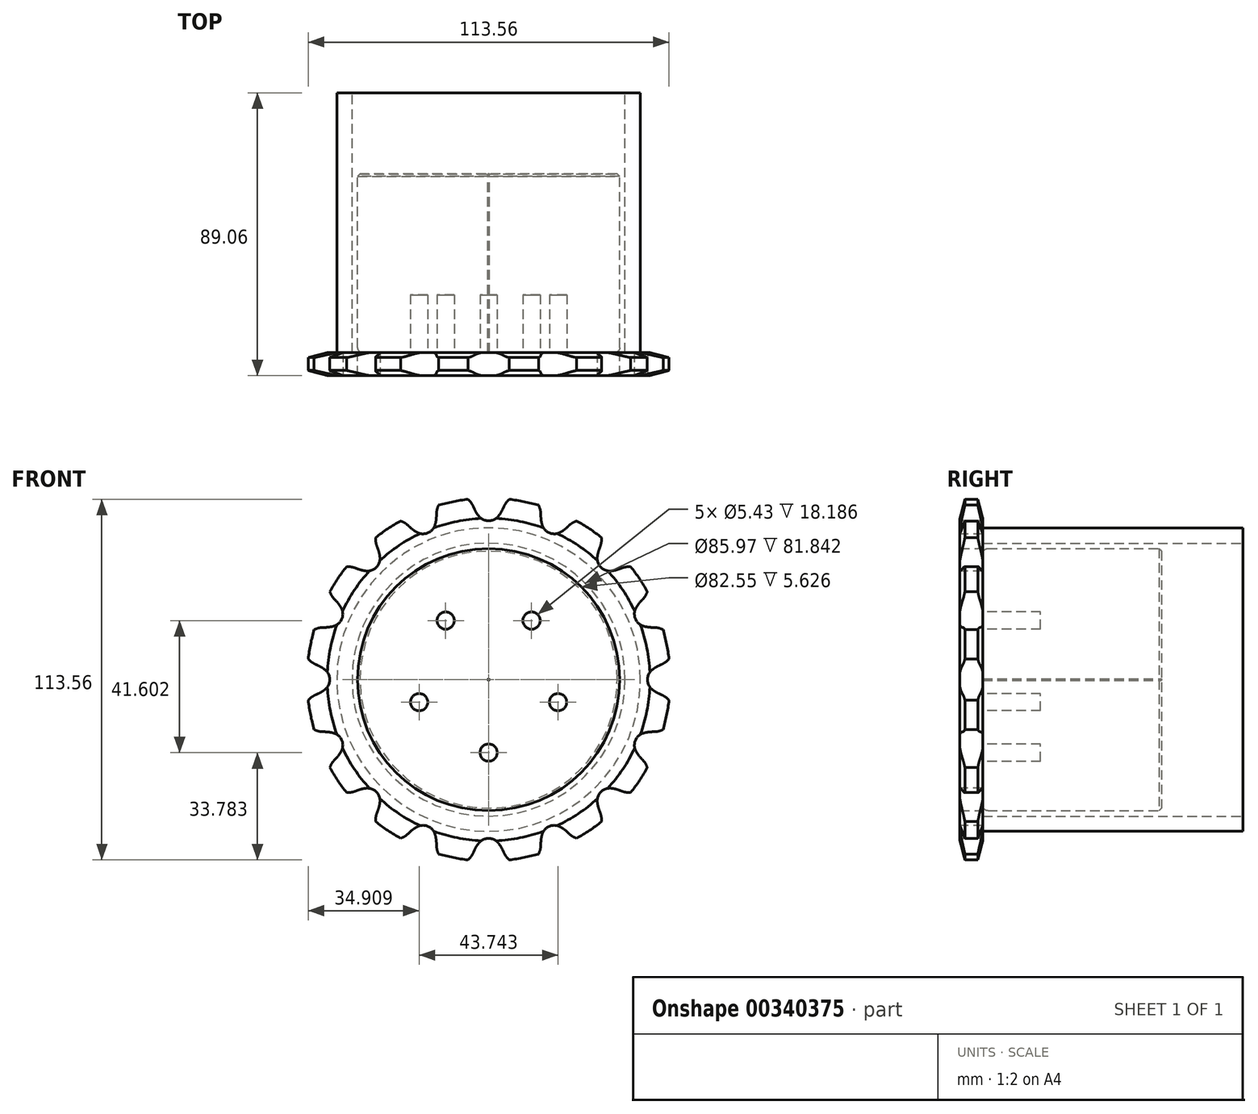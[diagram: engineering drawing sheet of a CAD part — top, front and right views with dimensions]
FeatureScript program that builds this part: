
annotation { "Feature Type Name" : "Feature", "Feature Type Description" : "" }
export const myFeature = defineFeature(function(context is Context, id is Id, definition is map)
    precondition{}
    {
        {
            var Q0;
            Q0=qCreatedBy(makeId("Right.planeOp"),FACE);
            var sketch = newSketch(context, id + "F0", { "sketchPlane" : qUnion([Q0])});
            skLineSegment(sketch, "E0", {"start": v(41.18, 0) * mm, "end": v(-36.1, 0) * mm, "construction": true});
            skLineSegment(sketch, "E1.bottom", {"start": v(-22.32, 0.21) * mm, "end": v(-15.1, 0.21) * mm});
            skLineSegment(sketch, "E1.top", {"start": v(-22.32, 57.15) * mm, "end": v(-15.1, 57.15) * mm});
            skLineSegment(sketch, "E1.left", {"start": v(-22.32, 0.21) * mm, "end": v(-22.32, 57.15) * mm});
            skLineSegment(sketch, "E1.right", {"start": v(-15.1, 0.21) * mm, "end": v(-15.1, 57.15) * mm});
            skLineSegment(sketch, "E2.bottom", {"start": v(-22.32, 0.21) * mm, "end": v(41.18, 0.21) * mm});
            skLineSegment(sketch, "E2.top", {"start": v(-22.32, 41.27) * mm, "end": v(41.18, 41.27) * mm});
            skLineSegment(sketch, "E2.left", {"start": v(-22.32, 0.21) * mm, "end": v(-22.32, 41.27) * mm});
            skLineSegment(sketch, "E2.right", {"start": v(41.18, 0.21) * mm, "end": v(41.18, 41.28) * mm});
            skLineSegment(sketch, "E3.MirrorCS", {"start": v(-22.32, -0.21) * mm, "end": v(-15.1, -0.21) * mm});
            skLineSegment(sketch, "E4.MirrorCS", {"start": v(41.18, -0.21) * mm, "end": v(41.18, -41.28) * mm});
            skLineSegment(sketch, "E5.MirrorCS", {"start": v(-22.32, -0.21) * mm, "end": v(-22.32, -41.27) * mm});
            skLineSegment(sketch, "E6.MirrorCS", {"start": v(-22.32, -57.15) * mm, "end": v(-15.1, -57.15) * mm});
            skLineSegment(sketch, "E7.MirrorCS", {"start": v(-22.32, -0.21) * mm, "end": v(-22.32, -57.15) * mm});
            skLineSegment(sketch, "E8.MirrorCS", {"start": v(-15.1, -0.21) * mm, "end": v(-15.1, -57.15) * mm});
            skLineSegment(sketch, "E9.MirrorCS", {"start": v(-22.32, -0.21) * mm, "end": v(41.18, -0.21) * mm});
            skLineSegment(sketch, "E10.MirrorCS", {"start": v(-22.32, -41.28) * mm, "end": v(41.18, -41.28) * mm});
            skLineSegment(sketch, "E11.left", {"start": v(-22.32, 32.14) * mm, "end": v(-22.32, 28.98) * mm});
            skLineSegment(sketch, "E12", {"start": v(-15.1, -42.98) * mm, "end": v(66.74, -42.98) * mm});
            skLineSegment(sketch, "E13", {"start": v(66.74, -32.66) * mm, "end": v(66.74, -47.8) * mm});
            skLineSegment(sketch, "E14", {"start": v(66.74, -47.8) * mm, "end": v(-15.1, -47.8) * mm});
            skSolve(sketch);
        }
        {
            var Q0;
            {var subQ0=sQuery(id+"F0.wireOp",EDGE,"E4.MirrorCS");Q0=makeQuery(id+"F0.imprint","IMPRINT",FACE,{"disambiguationData":[TD([[makeQuery(id+"F0.imprint","IMPRINT",EDGE,{"derivedFrom":subQ0}),-1.0]])]});}
            var Q1;
            {var subQ0=sQuery(id+"F0.wireOp",EDGE,"E6.MirrorCS");Q1=makeQuery(id+"F0.imprint","IMPRINT",FACE,{"disambiguationData":[TD([[makeQuery(id+"F0.imprint","IMPRINT",EDGE,{"derivedFrom":subQ0}),1.0]])]});}
            var Q2;
            {var subQ0=sQuery(id+"F0.wireOp",EDGE,"E9.MirrorCS");var subQ1=sQuery(id+"F0.wireOp",EDGE,"E7.MirrorCS");var subQ2=makeQuery(id+"F0.imprint","INTERSECT",VERTEX,{"derivedFrom":[subQ1,subQ0]});Q2=makeQuery(id+"F0.imprint","IMPRINT",FACE,{"disambiguationData":[TD([[makeQuery(id+"F0.imprint","IMPRINT",EDGE,{"disambiguationData":[TD([[subQ2,-1.0]])],"derivedFrom":subQ1}),1.0]])]});}
            var Q3;
            {var subQ0=sQuery(id+"F0.wireOp",EDGE,"E12");Q3=makeQuery(id+"F0.imprint","IMPRINT",FACE,{"disambiguationData":[TD([[makeQuery(id+"F0.imprint","IMPRINT",EDGE,{"derivedFrom":subQ0}),-1.0]])]});}
            var Q4;
            Q4=sQuery(id+"F0.wireOp",EDGE,"E0");
            revolve(context, id + "F1", {"entities" : qUnion([Q0, Q1, Q2, Q3]), "axis" : qUnion([Q4]), "revolveType" : RevolveType.FULL});
        }
        {
            var Q0;
            Q0=makeQuery(id+"F1.opRevolve","SWEPT_EDGE",EDGE,{"disambiguationData":[OSD([sQuery(id+"F0.wireOp",EDGE,"E8.MirrorCS"),sQuery(id+"F0.wireOp",EDGE,"E10.MirrorCS")])]});
            fillet(context, id + "F2", {"entities" : qUnion([Q0]), "radius" : 1.59 * mm, "tangentPropagation" : true, "allowEdgeOverflow" : false});
        }
        {
            var Q0;
            Q0=makeQuery(id+"F1.opRevolve","SWEPT_EDGE",EDGE,{"disambiguationData":[OSD([sQuery(id+"F0.wireOp",EDGE,"E4.MirrorCS"),sQuery(id+"F0.wireOp",EDGE,"E10.MirrorCS")])]});
            chamfer(context, id + "F3", {"entities" : qUnion([Q0]), "width" : 0.8 * mm, "tangentPropagation" : true});
        }
        {
            var Q0;
            Q0=makeQuery(id+"F1.opRevolve","SWEPT_EDGE",EDGE,{"disambiguationData":[OSD([sQuery(id+"F0.wireOp",EDGE,"E6.MirrorCS"),sQuery(id+"F0.wireOp",EDGE,"E8.MirrorCS")])]});
            var Q1;
            Q1=makeQuery(id+"F1.opRevolve","SWEPT_EDGE",EDGE,{"disambiguationData":[OSD([sQuery(id+"F0.wireOp",EDGE,"E6.MirrorCS"),sQuery(id+"F0.wireOp",EDGE,"E7.MirrorCS")])]});
            chamfer(context, id + "F4", {"entities" : qUnion([Q0, Q1]), "chamferType" : ChamferType.TWO_OFFSETS, "width1" : 6.35 * mm, "oppositeDirection" : false, "width2" : 1.57 * mm, "tangentPropagation" : true});
        }
        {
            var Q0;
            Q0=makeQuery(id+"F1.opRevolve","SWEPT_FACE",FACE,{"disambiguationData":[OSD([sQuery(id+"F0.wireOp",EDGE,"E7.MirrorCS")])]});
            var sketch = newSketch(context, id + "F5", { "sketchPlane" : qUnion([Q0])});
            skCircle(sketch, "E15", {"center": v(0, 0) * mm, "radius": 53.98 * mm, "construction": true});
            skLineSegment(sketch, "E16", {"start": v(0, 0) * mm, "end": v(0, 53.97) * mm, "construction": true});
            skLineSegment(sketch, "E17", {"start": v(43.52, 53.98) * mm, "end": v(0, 53.98) * mm, "construction": true});
            skLineSegment(sketch, "E18", {"start": v(0, 53.98) * mm, "end": v(5, 57.98) * mm, "construction": true});
            skLineSegment(sketch, "E19", {"start": v(5, 57.98) * mm, "end": v(-4.46, 53.73) * mm, "construction": true});
            skLineSegment(sketch, "E20", {"start": v(-4.46, 53.73) * mm, "end": v(-4.46, 53.73) * mm});
            skLineSegment(sketch, "E21", {"start": v(0, 0) * mm, "end": v(-11.6, 58.36) * mm, "construction": true});
            skArc(sketch, "E22", {"start": v(-11.6, 58.36) * mm, "mid": v(-17.32, 50.68) * mm, "end": v(-9.34, 45.4) * mm, "construction": true});
            skArc(sketch, "E23", {"start": v(-4.82, 54.52) * mm, "mid": v(-7.58, 57.55) * mm, "end": v(-11.6, 58.36) * mm});
            skArc(sketch, "E24", {"start": v(-9.34, 45.4) * mm, "mid": v(-4.92, 48.89) * mm, "end": v(-4.82, 54.52) * mm, "construction": true});
            skArc(sketch, "E25", {"start": v(-4.46, 53.73) * mm, "mid": v(-3.84, 52.57) * mm, "end": v(-3.1, 51.5) * mm});
            skArc(sketch, "E26", {"start": v(-3.1, 51.5) * mm, "mid": v(13.83, 63.4) * mm, "end": v(-4.46, 53.73) * mm, "construction": true});
            skLineSegment(sketch, "E27", {"start": v(9.34, 23.09) * mm, "end": v(-4.82, 54.52) * mm});
            skArc(sketch, "E28.MirrorCS", {"start": v(4.82, 54.52) * mm, "mid": v(7.58, 57.55) * mm, "end": v(11.6, 58.36) * mm});
            skLineSegment(sketch, "E29.MirrorCS", {"start": v(4.46, 53.73) * mm, "end": v(4.82, 54.52) * mm});
            skArc(sketch, "E30.MirrorCS", {"start": v(4.46, 53.73) * mm, "mid": v(3.84, 52.57) * mm, "end": v(3.1, 51.5) * mm});
            skLineSegment(sketch, "E31", {"start": v(3.1, 51.5) * mm, "end": v(3.1, 51.5) * mm});
            skLineSegment(sketch, "E32", {"start": v(-3.1, 51.5) * mm, "end": v(-3.1, 51.5) * mm});
            skArc(sketch, "E33", {"start": v(3.1, 51.5) * mm, "mid": v(0, 57.94) * mm, "end": v(-3.1, 51.5) * mm, "construction": true});
            skArc(sketch, "E34", {"start": v(-3.1, 51.5) * mm, "mid": v(0, 50.01) * mm, "end": v(3.1, 51.5) * mm});
            skArc(sketch, "E35.1.0", {"start": v(-44.81, -31.43) * mm, "mid": v(-46.05, -35.35) * mm, "end": v(-44.74, -39.23) * mm});
            skArc(sketch, "E35.1.1", {"start": v(-44.3, -30.72) * mm, "mid": v(-43.6, -29.61) * mm, "end": v(-43.05, -28.42) * mm});
            skArc(sketch, "E35.1.2", {"start": v(-43.05, -28.42) * mm, "mid": v(-43.31, -25) * mm, "end": v(-46.14, -23.07) * mm});
            skArc(sketch, "E35.1.3", {"start": v(-48.76, -23) * mm, "mid": v(-47.45, -22.95) * mm, "end": v(-46.14, -23.07) * mm});
            skLineSegment(sketch, "E35.1.4", {"start": v(-48.76, -23) * mm, "end": v(-49.63, -23.1) * mm});
            skArc(sketch, "E35.1.5", {"start": v(-49.63, -23.1) * mm, "mid": v(-53.64, -22.2) * mm, "end": v(-56.35, -19.13) * mm});
            skArc(sketch, "E35.2.0", {"start": v(49.63, -23.1) * mm, "mid": v(53.64, -22.2) * mm, "end": v(56.35, -19.13) * mm});
            skArc(sketch, "E35.2.1", {"start": v(48.76, -23) * mm, "mid": v(47.45, -22.95) * mm, "end": v(46.14, -23.07) * mm});
            skArc(sketch, "E35.2.2", {"start": v(46.14, -23.07) * mm, "mid": v(43.31, -25) * mm, "end": v(43.05, -28.42) * mm});
            skArc(sketch, "E35.2.3", {"start": v(44.3, -30.72) * mm, "mid": v(43.6, -29.61) * mm, "end": v(43.05, -28.42) * mm});
            skLineSegment(sketch, "E35.2.4", {"start": v(44.3, -30.72) * mm, "end": v(44.81, -31.43) * mm});
            skArc(sketch, "E35.2.5", {"start": v(44.81, -31.43) * mm, "mid": v(46.05, -35.35) * mm, "end": v(44.74, -39.23) * mm});
            skLineSegment(sketch, "E36", {"start": v(-4.82, 54.52) * mm, "end": v(-4.82, 54.52) * mm});
            skLineSegment(sketch, "E37", {"start": v(-4.46, 53.73) * mm, "end": v(-4.82, 54.52) * mm});
            skLineSegment(sketch, "E38", {"start": v(9.56, 22.61) * mm, "end": v(9.34, 23.09) * mm, "construction": true});
            skLineSegment(sketch, "E39", {"start": v(17.87, 4.16) * mm, "end": v(9.56, 22.61) * mm, "construction": true});
            skArc(sketch, "E40.1.0", {"start": v(-25.31, 48.53) * mm, "mid": v(-29.03, 50.27) * mm, "end": v(-33.06, 49.48) * mm});
            skLineSegment(sketch, "E40.1.1", {"start": v(-0.2, 24.9) * mm, "end": v(-25.31, 48.53) * mm});
            skArc(sketch, "E40.1.2", {"start": v(-24.68, 47.93) * mm, "mid": v(-23.67, 47.1) * mm, "end": v(-22.56, 46.4) * mm});
            skArc(sketch, "E40.1.3", {"start": v(-22.56, 46.4) * mm, "mid": v(-19.14, 46.2) * mm, "end": v(-16.85, 48.76) * mm});
            skArc(sketch, "E40.1.4", {"start": v(-16.44, 51.34) * mm, "mid": v(-16.56, 50.04) * mm, "end": v(-16.85, 48.76) * mm});
            skLineSegment(sketch, "E40.1.5", {"start": v(-16.44, 51.34) * mm, "end": v(-16.42, 52.22) * mm});
            skArc(sketch, "E40.1.6", {"start": v(-16.42, 52.22) * mm, "mid": v(-15.02, 56.08) * mm, "end": v(-11.6, 58.36) * mm});
            skArc(sketch, "E40.2.0", {"start": v(-41.96, 35.15) * mm, "mid": v(-46.06, 35.33) * mm, "end": v(-49.48, 33.06) * mm});
            skLineSegment(sketch, "E40.2.1", {"start": v(-9.72, 22.93) * mm, "end": v(-41.96, 35.15) * mm});
            skArc(sketch, "E40.2.2", {"start": v(-41.14, 34.84) * mm, "mid": v(-39.89, 34.45) * mm, "end": v(-38.6, 34.23) * mm});
            skArc(sketch, "E40.2.3", {"start": v(-38.6, 34.23) * mm, "mid": v(-35.36, 35.36) * mm, "end": v(-34.23, 38.6) * mm});
            skArc(sketch, "E40.2.4", {"start": v(-34.84, 41.14) * mm, "mid": v(-34.45, 39.89) * mm, "end": v(-34.23, 38.6) * mm});
            skLineSegment(sketch, "E40.2.5", {"start": v(-34.84, 41.14) * mm, "end": v(-35.15, 41.96) * mm});
            skArc(sketch, "E40.2.6", {"start": v(-35.15, 41.96) * mm, "mid": v(-35.33, 46.06) * mm, "end": v(-33.06, 49.48) * mm});
            skArc(sketch, "E40.3.0", {"start": v(-52.22, 16.42) * mm, "mid": v(-56.08, 15.02) * mm, "end": v(-58.36, 11.6) * mm});
            skLineSegment(sketch, "E40.3.1", {"start": v(-17.76, 17.47) * mm, "end": v(-52.22, 16.42) * mm});
            skArc(sketch, "E40.3.2", {"start": v(-51.34, 16.44) * mm, "mid": v(-50.04, 16.56) * mm, "end": v(-48.76, 16.85) * mm});
            skArc(sketch, "E40.3.3", {"start": v(-48.76, 16.85) * mm, "mid": v(-46.2, 19.14) * mm, "end": v(-46.4, 22.56) * mm});
            skArc(sketch, "E40.3.4", {"start": v(-47.93, 24.68) * mm, "mid": v(-47.1, 23.67) * mm, "end": v(-46.4, 22.56) * mm});
            skLineSegment(sketch, "E40.3.5", {"start": v(-47.93, 24.68) * mm, "end": v(-48.53, 25.31) * mm});
            skArc(sketch, "E40.3.6", {"start": v(-48.53, 25.31) * mm, "mid": v(-50.27, 29.03) * mm, "end": v(-49.48, 33.06) * mm});
            skArc(sketch, "E40.4.0", {"start": v(-54.52, -4.82) * mm, "mid": v(-57.55, -7.58) * mm, "end": v(-58.36, -11.6) * mm});
            skLineSegment(sketch, "E40.4.1", {"start": v(-23.09, 9.34) * mm, "end": v(-54.52, -4.82) * mm});
            skArc(sketch, "E40.4.2", {"start": v(-53.73, -4.46) * mm, "mid": v(-52.57, -3.84) * mm, "end": v(-51.5, -3.1) * mm});
            skArc(sketch, "E40.4.3", {"start": v(-51.5, -3.1) * mm, "mid": v(-50.01, 0) * mm, "end": v(-51.5, 3.1) * mm});
            skArc(sketch, "E40.4.4", {"start": v(-53.73, 4.46) * mm, "mid": v(-52.57, 3.84) * mm, "end": v(-51.5, 3.1) * mm});
            skLineSegment(sketch, "E40.4.5", {"start": v(-53.73, 4.46) * mm, "end": v(-54.52, 4.82) * mm});
            skArc(sketch, "E40.4.6", {"start": v(-54.52, 4.82) * mm, "mid": v(-57.55, 7.58) * mm, "end": v(-58.36, 11.6) * mm});
            skArc(sketch, "E40.5.0", {"start": v(-48.53, -25.31) * mm, "mid": v(-50.27, -29.03) * mm, "end": v(-49.48, -33.06) * mm});
            skLineSegment(sketch, "E40.5.1", {"start": v(-24.9, -0.2) * mm, "end": v(-48.53, -25.31) * mm});
            skArc(sketch, "E40.5.2", {"start": v(-47.93, -24.68) * mm, "mid": v(-47.1, -23.67) * mm, "end": v(-46.4, -22.56) * mm});
            skArc(sketch, "E40.5.3", {"start": v(-46.4, -22.56) * mm, "mid": v(-46.2, -19.14) * mm, "end": v(-48.76, -16.85) * mm});
            skArc(sketch, "E40.5.4", {"start": v(-51.34, -16.44) * mm, "mid": v(-50.04, -16.56) * mm, "end": v(-48.76, -16.85) * mm});
            skLineSegment(sketch, "E40.5.5", {"start": v(-51.34, -16.44) * mm, "end": v(-52.22, -16.42) * mm});
            skArc(sketch, "E40.5.6", {"start": v(-52.22, -16.42) * mm, "mid": v(-56.08, -15.02) * mm, "end": v(-58.36, -11.6) * mm});
            skArc(sketch, "E40.6.0", {"start": v(-35.15, -41.96) * mm, "mid": v(-35.33, -46.06) * mm, "end": v(-33.06, -49.48) * mm});
            skLineSegment(sketch, "E40.6.1", {"start": v(-22.93, -9.72) * mm, "end": v(-35.15, -41.96) * mm});
            skArc(sketch, "E40.6.2", {"start": v(-34.84, -41.14) * mm, "mid": v(-34.45, -39.89) * mm, "end": v(-34.23, -38.6) * mm});
            skArc(sketch, "E40.6.3", {"start": v(-34.23, -38.6) * mm, "mid": v(-35.36, -35.36) * mm, "end": v(-38.6, -34.23) * mm});
            skArc(sketch, "E40.6.4", {"start": v(-41.14, -34.84) * mm, "mid": v(-39.89, -34.45) * mm, "end": v(-38.6, -34.23) * mm});
            skLineSegment(sketch, "E40.6.5", {"start": v(-41.14, -34.84) * mm, "end": v(-41.96, -35.15) * mm});
            skArc(sketch, "E40.6.6", {"start": v(-41.96, -35.15) * mm, "mid": v(-46.06, -35.33) * mm, "end": v(-49.48, -33.06) * mm});
            skArc(sketch, "E40.7.0", {"start": v(-16.42, -52.22) * mm, "mid": v(-15.02, -56.08) * mm, "end": v(-11.6, -58.36) * mm});
            skLineSegment(sketch, "E40.7.1", {"start": v(-17.47, -17.76) * mm, "end": v(-16.42, -52.22) * mm});
            skArc(sketch, "E40.7.2", {"start": v(-16.44, -51.34) * mm, "mid": v(-16.56, -50.04) * mm, "end": v(-16.85, -48.76) * mm});
            skArc(sketch, "E40.7.3", {"start": v(-16.85, -48.76) * mm, "mid": v(-19.14, -46.2) * mm, "end": v(-22.56, -46.4) * mm});
            skArc(sketch, "E40.7.4", {"start": v(-24.68, -47.93) * mm, "mid": v(-23.67, -47.1) * mm, "end": v(-22.56, -46.4) * mm});
            skLineSegment(sketch, "E40.7.5", {"start": v(-24.68, -47.93) * mm, "end": v(-25.31, -48.53) * mm});
            skArc(sketch, "E40.7.6", {"start": v(-25.31, -48.53) * mm, "mid": v(-29.03, -50.27) * mm, "end": v(-33.06, -49.48) * mm});
            skArc(sketch, "E40.8.0", {"start": v(4.82, -54.52) * mm, "mid": v(7.58, -57.55) * mm, "end": v(11.6, -58.36) * mm});
            skLineSegment(sketch, "E40.8.1", {"start": v(-9.34, -23.09) * mm, "end": v(4.82, -54.52) * mm});
            skArc(sketch, "E40.8.2", {"start": v(4.46, -53.73) * mm, "mid": v(3.84, -52.57) * mm, "end": v(3.1, -51.5) * mm});
            skArc(sketch, "E40.8.3", {"start": v(3.1, -51.5) * mm, "mid": v(0, -50.01) * mm, "end": v(-3.1, -51.5) * mm});
            skArc(sketch, "E40.8.4", {"start": v(-4.46, -53.73) * mm, "mid": v(-3.84, -52.57) * mm, "end": v(-3.1, -51.5) * mm});
            skLineSegment(sketch, "E40.8.5", {"start": v(-4.46, -53.73) * mm, "end": v(-4.82, -54.52) * mm});
            skArc(sketch, "E40.8.6", {"start": v(-4.82, -54.52) * mm, "mid": v(-7.58, -57.55) * mm, "end": v(-11.6, -58.36) * mm});
            skArc(sketch, "E40.9.0", {"start": v(25.31, -48.53) * mm, "mid": v(29.03, -50.27) * mm, "end": v(33.06, -49.48) * mm});
            skLineSegment(sketch, "E40.9.1", {"start": v(0.2, -24.9) * mm, "end": v(25.31, -48.53) * mm});
            skArc(sketch, "E40.9.2", {"start": v(24.68, -47.93) * mm, "mid": v(23.67, -47.1) * mm, "end": v(22.56, -46.4) * mm});
            skArc(sketch, "E40.9.3", {"start": v(22.56, -46.4) * mm, "mid": v(19.14, -46.2) * mm, "end": v(16.85, -48.76) * mm});
            skArc(sketch, "E40.9.4", {"start": v(16.44, -51.34) * mm, "mid": v(16.56, -50.04) * mm, "end": v(16.85, -48.76) * mm});
            skLineSegment(sketch, "E40.9.5", {"start": v(16.44, -51.34) * mm, "end": v(16.42, -52.22) * mm});
            skArc(sketch, "E40.9.6", {"start": v(16.42, -52.22) * mm, "mid": v(15.02, -56.08) * mm, "end": v(11.6, -58.36) * mm});
            skArc(sketch, "E40.10.0", {"start": v(41.96, -35.15) * mm, "mid": v(46.06, -35.33) * mm, "end": v(49.48, -33.06) * mm});
            skLineSegment(sketch, "E40.10.1", {"start": v(9.72, -22.93) * mm, "end": v(41.96, -35.15) * mm});
            skArc(sketch, "E40.10.2", {"start": v(41.14, -34.84) * mm, "mid": v(39.89, -34.45) * mm, "end": v(38.6, -34.23) * mm});
            skArc(sketch, "E40.10.3", {"start": v(38.6, -34.23) * mm, "mid": v(35.36, -35.36) * mm, "end": v(34.23, -38.6) * mm});
            skArc(sketch, "E40.10.4", {"start": v(34.84, -41.14) * mm, "mid": v(34.45, -39.89) * mm, "end": v(34.23, -38.6) * mm});
            skLineSegment(sketch, "E40.10.5", {"start": v(34.84, -41.14) * mm, "end": v(35.15, -41.96) * mm});
            skArc(sketch, "E40.10.6", {"start": v(35.15, -41.96) * mm, "mid": v(35.33, -46.06) * mm, "end": v(33.06, -49.48) * mm});
            skArc(sketch, "E40.11.0", {"start": v(52.22, -16.42) * mm, "mid": v(56.08, -15.02) * mm, "end": v(58.36, -11.6) * mm});
            skLineSegment(sketch, "E40.11.1", {"start": v(17.76, -17.47) * mm, "end": v(52.22, -16.42) * mm});
            skArc(sketch, "E40.11.2", {"start": v(51.34, -16.44) * mm, "mid": v(50.04, -16.56) * mm, "end": v(48.76, -16.85) * mm});
            skArc(sketch, "E40.11.3", {"start": v(48.76, -16.85) * mm, "mid": v(46.2, -19.14) * mm, "end": v(46.4, -22.56) * mm});
            skArc(sketch, "E40.11.4", {"start": v(47.93, -24.68) * mm, "mid": v(47.1, -23.67) * mm, "end": v(46.4, -22.56) * mm});
            skLineSegment(sketch, "E40.11.5", {"start": v(47.93, -24.68) * mm, "end": v(48.53, -25.31) * mm});
            skArc(sketch, "E40.11.6", {"start": v(48.53, -25.31) * mm, "mid": v(50.27, -29.03) * mm, "end": v(49.48, -33.06) * mm});
            skArc(sketch, "E40.12.0", {"start": v(54.52, 4.82) * mm, "mid": v(57.55, 7.58) * mm, "end": v(58.36, 11.6) * mm});
            skLineSegment(sketch, "E40.12.1", {"start": v(23.09, -9.34) * mm, "end": v(54.52, 4.82) * mm});
            skArc(sketch, "E40.12.2", {"start": v(53.73, 4.46) * mm, "mid": v(52.57, 3.84) * mm, "end": v(51.5, 3.1) * mm});
            skArc(sketch, "E40.12.3", {"start": v(51.5, 3.1) * mm, "mid": v(50.01, 0) * mm, "end": v(51.5, -3.1) * mm});
            skArc(sketch, "E40.12.4", {"start": v(53.73, -4.46) * mm, "mid": v(52.57, -3.84) * mm, "end": v(51.5, -3.1) * mm});
            skLineSegment(sketch, "E40.12.5", {"start": v(53.73, -4.46) * mm, "end": v(54.52, -4.82) * mm});
            skArc(sketch, "E40.12.6", {"start": v(54.52, -4.82) * mm, "mid": v(57.55, -7.58) * mm, "end": v(58.36, -11.6) * mm});
            skArc(sketch, "E40.13.0", {"start": v(48.53, 25.31) * mm, "mid": v(50.27, 29.03) * mm, "end": v(49.48, 33.06) * mm});
            skLineSegment(sketch, "E40.13.1", {"start": v(24.9, 0.2) * mm, "end": v(48.53, 25.31) * mm});
            skArc(sketch, "E40.13.2", {"start": v(47.93, 24.68) * mm, "mid": v(47.1, 23.67) * mm, "end": v(46.4, 22.56) * mm});
            skArc(sketch, "E40.13.3", {"start": v(46.4, 22.56) * mm, "mid": v(46.2, 19.14) * mm, "end": v(48.76, 16.85) * mm});
            skArc(sketch, "E40.13.4", {"start": v(51.34, 16.44) * mm, "mid": v(50.04, 16.56) * mm, "end": v(48.76, 16.85) * mm});
            skLineSegment(sketch, "E40.13.5", {"start": v(51.34, 16.44) * mm, "end": v(52.22, 16.42) * mm});
            skArc(sketch, "E40.13.6", {"start": v(52.22, 16.42) * mm, "mid": v(56.08, 15.02) * mm, "end": v(58.36, 11.6) * mm});
            skArc(sketch, "E40.14.0", {"start": v(35.15, 41.96) * mm, "mid": v(35.33, 46.06) * mm, "end": v(33.06, 49.48) * mm});
            skLineSegment(sketch, "E40.14.1", {"start": v(22.93, 9.72) * mm, "end": v(35.15, 41.96) * mm});
            skArc(sketch, "E40.14.2", {"start": v(34.84, 41.14) * mm, "mid": v(34.45, 39.89) * mm, "end": v(34.23, 38.6) * mm});
            skArc(sketch, "E40.14.3", {"start": v(34.23, 38.6) * mm, "mid": v(35.36, 35.36) * mm, "end": v(38.6, 34.23) * mm});
            skArc(sketch, "E40.14.4", {"start": v(41.14, 34.84) * mm, "mid": v(39.89, 34.45) * mm, "end": v(38.6, 34.23) * mm});
            skLineSegment(sketch, "E40.14.5", {"start": v(41.14, 34.84) * mm, "end": v(41.96, 35.15) * mm});
            skArc(sketch, "E40.14.6", {"start": v(41.96, 35.15) * mm, "mid": v(46.06, 35.33) * mm, "end": v(49.48, 33.06) * mm});
            skArc(sketch, "E40.15.0", {"start": v(16.42, 52.22) * mm, "mid": v(15.02, 56.08) * mm, "end": v(11.6, 58.36) * mm});
            skLineSegment(sketch, "E40.15.1", {"start": v(17.47, 17.76) * mm, "end": v(16.42, 52.22) * mm});
            skArc(sketch, "E40.15.2", {"start": v(16.44, 51.34) * mm, "mid": v(16.56, 50.04) * mm, "end": v(16.85, 48.76) * mm});
            skArc(sketch, "E40.15.3", {"start": v(16.85, 48.76) * mm, "mid": v(19.14, 46.2) * mm, "end": v(22.56, 46.4) * mm});
            skArc(sketch, "E40.15.4", {"start": v(24.68, 47.93) * mm, "mid": v(23.67, 47.1) * mm, "end": v(22.56, 46.4) * mm});
            skLineSegment(sketch, "E40.15.5", {"start": v(24.68, 47.93) * mm, "end": v(25.31, 48.53) * mm});
            skArc(sketch, "E40.15.6", {"start": v(25.31, 48.53) * mm, "mid": v(29.03, 50.27) * mm, "end": v(33.06, 49.48) * mm});
            skSolve(sketch);
        }
        {
            var Q0;
            Q0=qSketchRegion(id+"F5",true);
            extrude(context, id + "F6", {"entities" : qUnion([Q0]), "operationType" : NewBodyOperationType.INTERSECT, "endBound" : BoundingType.THROUGH_ALL, "oppositeDirection" : true, "depth" : 35.05 * mm});
        }
        {
            var Q0;
            Q0=makeQuery(id+"F1.opRevolve","SWEPT_FACE",FACE,{"disambiguationData":[OSD([sQuery(id+"F0.wireOp",EDGE,"E7.MirrorCS")])]});
            var sketch = newSketch(context, id + "F7", { "sketchPlane" : qUnion([Q0])});
            skCircle(sketch, "E41", {"center": v(0, -23) * mm, "radius": 2.72 * mm});
            skCircle(sketch, "E42.1.0", {"center": v(21.87, -7.1) * mm, "radius": 2.72 * mm});
            skCircle(sketch, "E42.2.0", {"center": v(13.52, 18.6) * mm, "radius": 2.72 * mm});
            skCircle(sketch, "E42.3.0", {"center": v(-13.52, 18.6) * mm, "radius": 2.72 * mm});
            skCircle(sketch, "E42.4.0", {"center": v(-21.87, -7.1) * mm, "radius": 2.72 * mm});
            skPoint(sketch, "E42.center", {"position": v(0, 0) * mm});
            skSolve(sketch);
        }
        {
            var Q0;
            Q0 = qSketchRegion(id + "F7", true);
            extrude(context, id + "F8", {"entities" : qUnion([Q0]), "operationType" : NewBodyOperationType.REMOVE, "oppositeDirection" : true, "depth" : 25.4 * mm});
        }
    });
